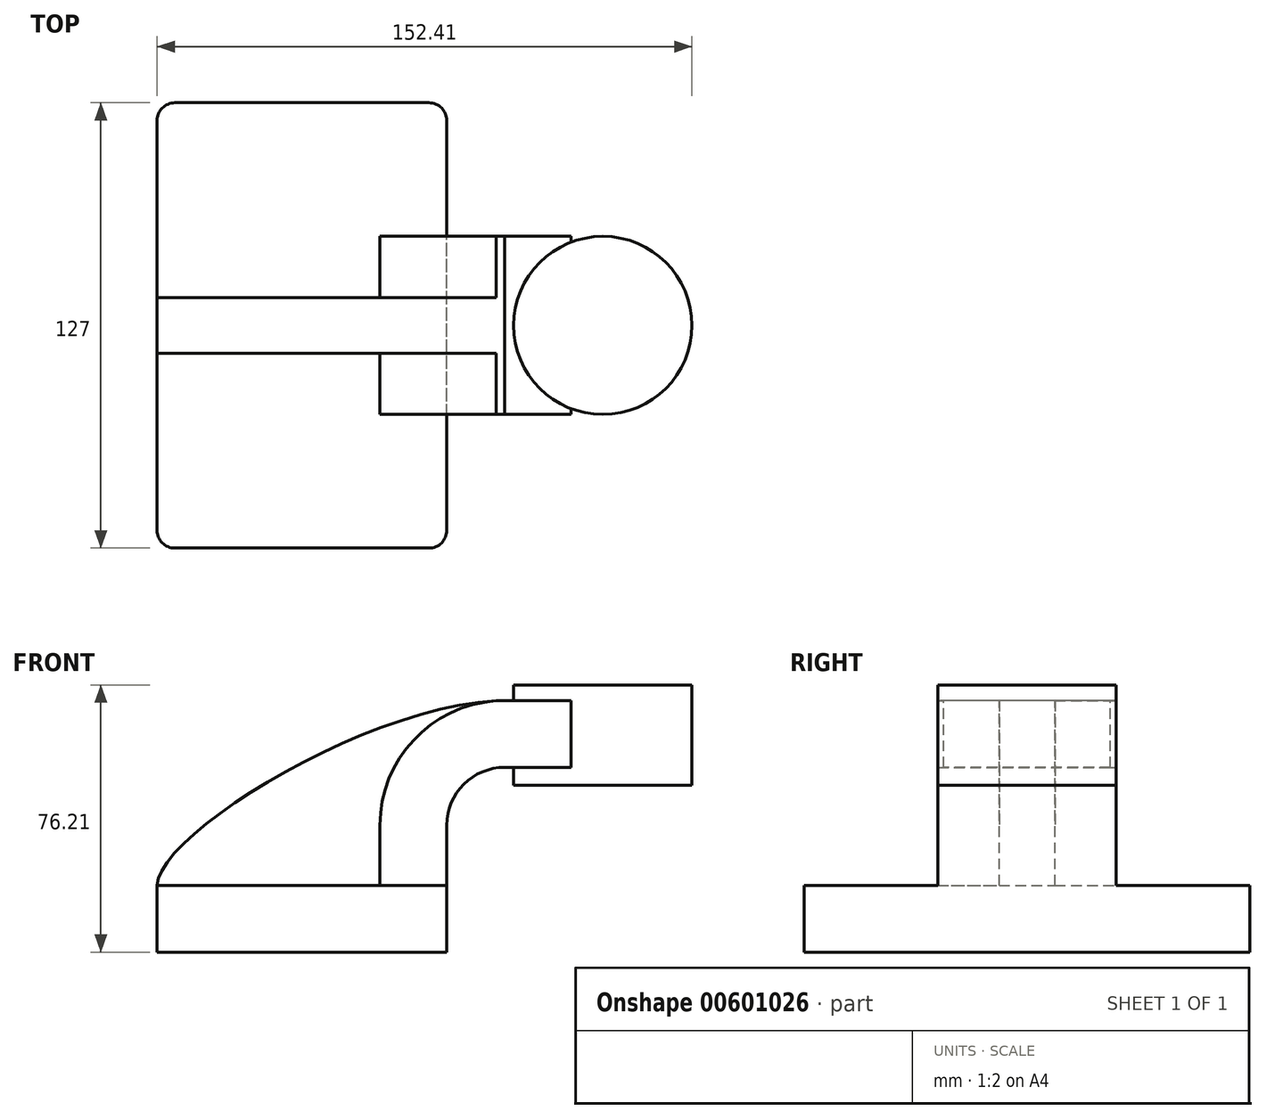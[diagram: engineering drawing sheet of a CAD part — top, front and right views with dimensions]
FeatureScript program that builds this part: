
annotation { "Feature Type Name" : "Feature", "Feature Type Description" : "" }
export const myFeature = defineFeature(function(context is Context, id is Id, definition is map)
    precondition{}
    {
        {
            var Q0;
            Q0=qCreatedBy(makeId("Front.planeOp"),FACE);
            var sketch = newSketch(context, id + "F0", { "sketchPlane" : qUnion([Q0])});
            skLineSegment(sketch, "E0.bottom", {"start": v(41.28, -9.52) * mm, "end": v(-41.28, -9.53) * mm});
            skLineSegment(sketch, "E0.top", {"start": v(41.28, 9.53) * mm, "end": v(-41.28, 9.52) * mm});
            skLineSegment(sketch, "E0.left", {"start": v(41.28, -9.52) * mm, "end": v(41.28, 9.53) * mm});
            skLineSegment(sketch, "E0.right", {"start": v(-41.28, -9.53) * mm, "end": v(-41.28, 9.52) * mm});
            skPoint(sketch, "E0.middle", {"position": v(0, 0) * mm});
            skLineSegment(sketch, "E1", {"start": v(41.28, 9.53) * mm, "end": v(41.28, 26.65) * mm});
            skArc(sketch, "E2", {"start": v(41.28, 26.65) * mm, "mid": v(46.11, 38.33) * mm, "end": v(57.79, 43.16) * mm});
            skLineSegment(sketch, "E3.bottom", {"start": v(111.12, 38.1) * mm, "end": v(60.32, 38.1) * mm});
            skLineSegment(sketch, "E3.top", {"start": v(111.12, 66.68) * mm, "end": v(60.32, 66.68) * mm});
            skLineSegment(sketch, "E3.left", {"start": v(111.12, 38.1) * mm, "end": v(111.12, 66.67) * mm});
            skLineSegment(sketch, "E3.right", {"start": v(60.32, 38.1) * mm, "end": v(60.32, 66.67) * mm});
            skPoint(sketch, "E3.middle", {"position": v(85.72, 52.39) * mm});
            skLineSegment(sketch, "E4", {"start": v(57.79, 43.16) * mm, "end": v(76.67, 43.16) * mm});
            skLineSegment(sketch, "E5.0", {"start": v(57.79, 62.21) * mm, "end": v(76.67, 62.21) * mm});
            skArc(sketch, "E5.1", {"start": v(22.23, 26.65) * mm, "mid": v(32.64, 51.8) * mm, "end": v(57.79, 62.21) * mm});
            skLineSegment(sketch, "E5.2", {"start": v(22.23, 9.53) * mm, "end": v(22.23, 26.65) * mm});
            skLineSegment(sketch, "E6", {"start": v(76.67, 43.16) * mm, "end": v(76.67, 62.21) * mm});
            skFitSpline(sketch, "E7", {"points": [v(-41.28, 9.52) * mm, v(57.79, 62.21) * mm], "startDerivative": vector(0.94, 43.81) * mm, "endDerivative": vector(115.43, 1.73) * mm});
            skLineSegment(sketch, "E8", {"start": v(85.72, 70.33) * mm, "end": v(85.72, 34.05) * mm});
            skPoint(sketch, "E8.startSnap0", {"position": v(85.72, 66.68) * mm});
            skPoint(sketch, "E8.endSnap0", {"position": v(85.72, 38.1) * mm});
            skSolve(sketch);
        }
        {
            var Q0;
            Q0=makeQuery(id+"F0.imprint","IMPRINT",FACE,{"disambiguationData":[TD([[makeQuery(id+"F0.imprint","IMPRINT",EDGE,{"derivedFrom":sQuery(id+"F0.wireOp",EDGE,"E0.bottom")}),-1.0]])]});
            extrude(context, id + "F1", {"entities" : qUnion([Q0]), "endBound" : BoundingType.SYMMETRIC, "depth" : 127 * mm, "offsetDistance" : 25.4 * mm});
        }
        {
            var Q0;
            {var subQ0=sQuery(id+"F0.wireOp",EDGE,"E1");Q0=makeQuery(id+"F0.imprint","IMPRINT",FACE,{"disambiguationData":[TD([[makeQuery(id+"F0.imprint","IMPRINT",EDGE,{"derivedFrom":subQ0}),1.0]])]});}
            var Q1;
            {var subQ5=sQuery(id+"F0.wireOp",EDGE,"E6");Q1=makeQuery(id+"F0.imprint","IMPRINT",FACE,{"disambiguationData":[TD([[makeQuery(id+"F0.imprint","IMPRINT",EDGE,{"derivedFrom":subQ5}),1.0]])]});}
            extrude(context, id + "F2", {"entities" : qUnion([Q0, Q1]), "operationType" : NewBodyOperationType.ADD, "endBound" : BoundingType.SYMMETRIC, "depth" : 50.8 * mm, "offsetDistance" : 25.4 * mm});
        }
        {
            var Q0;
            {var subQ3=sQuery(id+"F0.wireOp",EDGE,"E5.2");Q0=makeQuery(id+"F0.imprint","IMPRINT",FACE,{"disambiguationData":[TD([[makeQuery(id+"F0.imprint","IMPRINT",EDGE,{"derivedFrom":subQ3}),1.0]])]});}
            extrude(context, id + "F3", {"entities" : qUnion([Q0]), "operationType" : NewBodyOperationType.ADD, "endBound" : BoundingType.SYMMETRIC, "depth" : 15.88 * mm, "offsetDistance" : 25.4 * mm});
        }
        {
            var Q0;
            {var subQ0=sQuery(id+"F0.wireOp",EDGE,"E3.left");Q0=makeQuery(id+"F0.imprint","IMPRINT",FACE,{"disambiguationData":[TD([[makeQuery(id+"F0.imprint","IMPRINT",EDGE,{"derivedFrom":subQ0}),1.0]])]});}
            var Q1;
            Q1=sQuery(id+"F0.wireOp",EDGE,"E8");
            revolve(context, id + "F4", {"operationType" : NewBodyOperationType.ADD, "entities" : qUnion([Q0]), "axis" : qUnion([Q1]), "revolveType" : RevolveType.FULL});
        }
        {
            var Q0;
            Q0=makeQuery(id+"F1.opExtrude","CAP_EDGE",EDGE,{"disambiguationData":[OSD([sQuery(id+"F0.wireOp",EDGE,"E0.left")])],"isStart":false});
            var Q1;
            Q1=makeQuery(id+"F1.opExtrude","CAP_EDGE",EDGE,{"disambiguationData":[OSD([sQuery(id+"F0.wireOp",EDGE,"E0.left")])],"isStart":true});
            var Q2;
            Q2=makeQuery(id+"F1.opExtrude","CAP_EDGE",EDGE,{"disambiguationData":[OSD([sQuery(id+"F0.wireOp",EDGE,"E0.right")])],"isStart":false});
            var Q3;
            Q3=makeQuery(id+"F1.opExtrude","CAP_EDGE",EDGE,{"disambiguationData":[OSD([sQuery(id+"F0.wireOp",EDGE,"E0.right")])],"isStart":true});
            fillet(context, id + "F5", {"entities" : qUnion([Q0, Q1, Q2, Q3]), "radius" : 5.08 * mm, "tangentPropagation" : true, "allowEdgeOverflow" : false});
        }
    });
